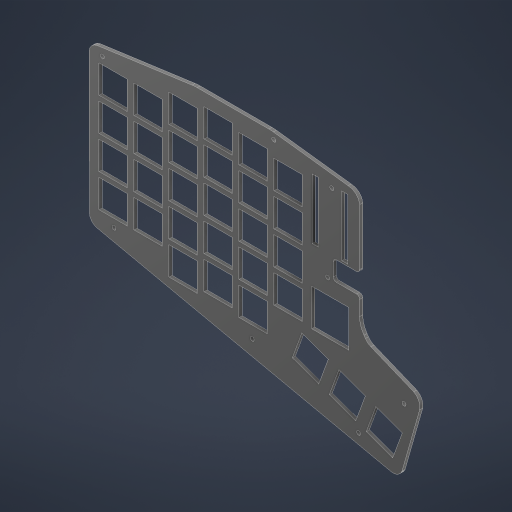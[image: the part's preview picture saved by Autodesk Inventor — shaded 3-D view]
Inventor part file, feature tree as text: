
AUTODESK INVENTOR PART (.ipt)
format: ipt  version: 2024.3 (Build 283343000, 343)  size: 539,648 bytes
history: native  units: in
note: dims shown in document units (in); Inventor stores cm internally (conversion verified against a paired STEP export)
features: other x3, plane x1, extrude x1, fillet x1, sketch x1, reference x1
ambient origin geometry x8: Origin, YZ Plane, XZ Plane, XY Plane, X Axis, Y Axis, Z Axis, Center Point
bodies: Solid1 (feature_tree)
feature tree (8):
  plane  "Work Plane1"
  extrude  "Extrusion1"  Depth=0.57in
  fillet  "Fillet1"  Radius=0.57in
  sketch  "Sketch1"  dims[d2=0.57in d3=0.57in d4=0.57in d5=0.57in d6=0.57in d7=0.57in d8=0.57in d9=0.57in d10=0.57in d11=0.57in d12=0.57in d13=0.57in d14=0.57in d15=0.57in d16=0.57in d17=0.57in d18=0.57in d19=0.57in d20=0.57in d21=0.57in d22=0.57in d23=0.57in d24=0.57in d25=0.57in d26=0.57in d27=0.57in d28=0.57in d29=0.57in d30=0.57in d31=0.57in d32=0.57in d33=0.57in d34=0.57in d35=0.57in d36=0.57in d37=0.57in d38=0.57in d39=0.57in d40=0.57in d41=0.57in d42=0.57in d43=0.57in d44=0.57in d45=0.57in d46=0.57in d47=0.57in d48=0.57in d49=0.57in d50=0.57in d51=0.57in d52=0.57in d53=0.57in d54=0.57in d55=0.57in d56=0.285in d57=0.57in d58=0.57in d59=0.285in d60=0.57in d61=0.57in d62=0.57in d63=0.57in d64=0.57in d65=0.57in d66=0.57in d67=0.57in d68=0.285in d69=0.285in d70=0.285in d71=0.285in d72=0.285in d73=0.285in d74=0.285in d75=0.285in d76=90.0deg d77=0.75in d78=0.75in d79=0.0625in d80=0.125in d81=0.0625in d82=0.0625in d83=0.125in d84=0.0625in d85=0.0625in d86=0.0625in d87=0.0in d88=0.0625in d91=0.0625in d92=0.0625in d93=0.0625in]
  reference  "Reference1"
  other  "<userpath>\Documents\GitHub\clackenPersonal\Case Cad\Main Case Assembly.iam"
  other  "Main Case Assembly.iam"
  other  "Split V2:1"
